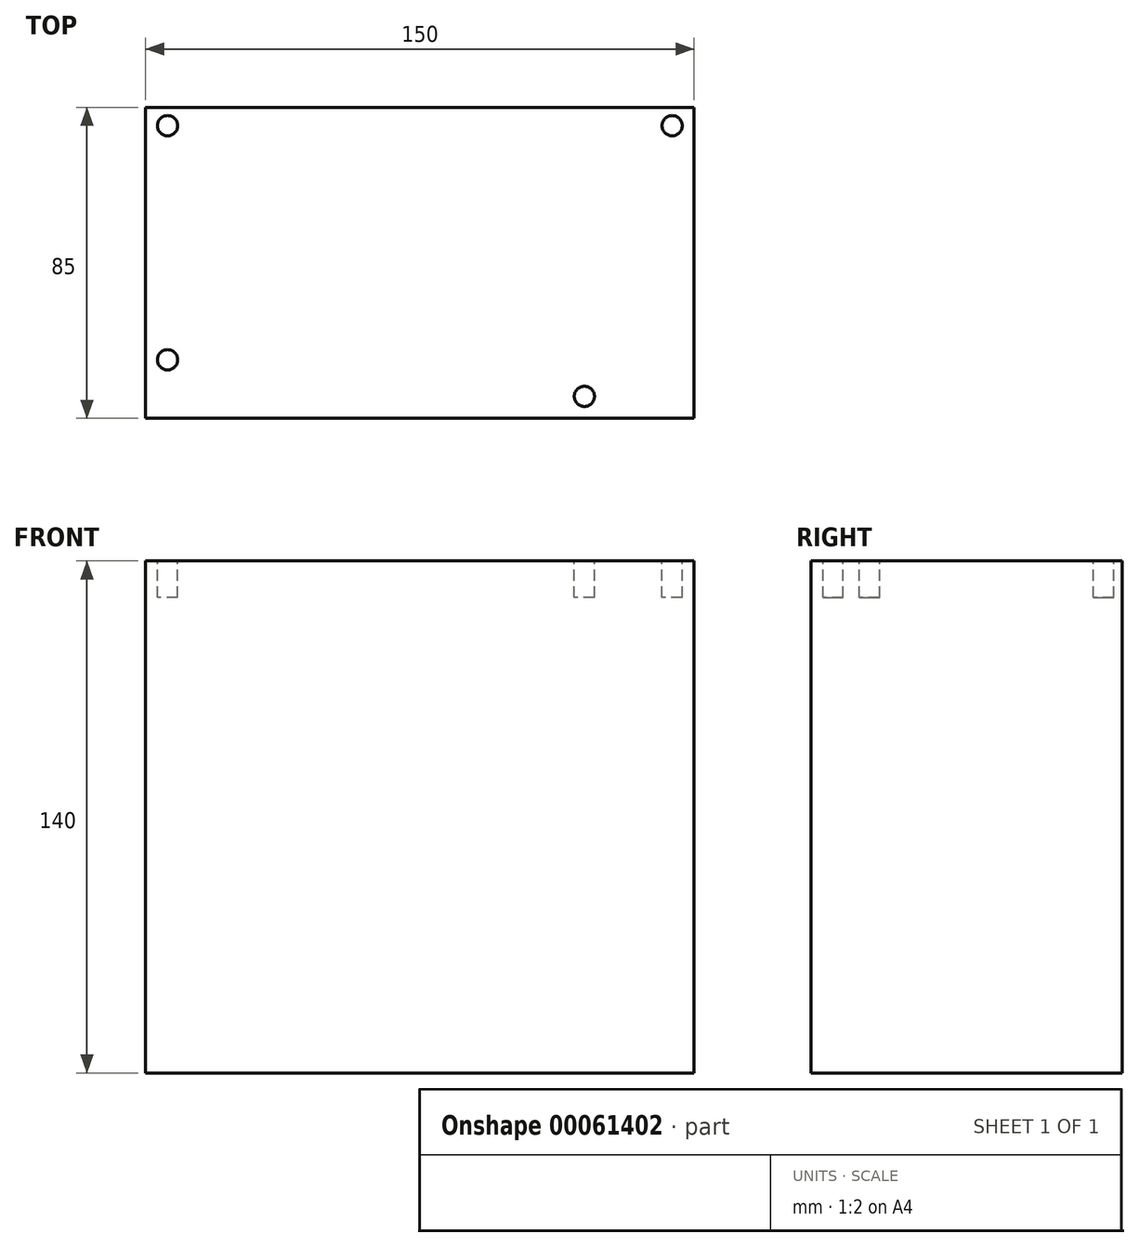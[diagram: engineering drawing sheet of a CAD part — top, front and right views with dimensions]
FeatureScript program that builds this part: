
annotation { "Feature Type Name" : "Feature", "Feature Type Description" : "" }
export const myFeature = defineFeature(function(context is Context, id is Id, definition is map)
    precondition{}
    {
        {
            var Q0;
            Q0=qCreatedBy(makeId("Front.planeOp"),FACE);
            var sketch = newSketch(context, id + "F0", { "sketchPlane" : qUnion([Q0])});
            skLineSegment(sketch, "E0.bottom", {"start": v(-73.07, 66.3) * mm, "end": v(76.93, 66.3) * mm});
            skLineSegment(sketch, "E0.top", {"start": v(-73.07, -73.7) * mm, "end": v(76.93, -73.7) * mm});
            skLineSegment(sketch, "E0.left", {"start": v(-73.07, 66.3) * mm, "end": v(-73.07, -73.7) * mm});
            skLineSegment(sketch, "E0.right", {"start": v(76.93, 66.3) * mm, "end": v(76.93, -73.7) * mm});
            skSolve(sketch);
        }
        {
            var Q0;
            Q0 = qSketchRegion(id + "F0", true);
            extrude(context, id + "F1", {"entities" : qUnion([Q0]), "depth" : 85 * mm});
        }
        {
            var Q0;
            Q0=makeQuery(id+"F1.opExtrude","SWEPT_FACE",FACE,{"disambiguationData":[OSD([sQuery(id+"F0.wireOp",EDGE,"E0.bottom")])]});
            var sketch = newSketch(context, id + "F2", { "sketchPlane" : qUnion([Q0])});
            skCircle(sketch, "E1", {"center": v(-67.07, -5) * mm, "radius": 2.77 * mm});
            skCircle(sketch, "E2", {"center": v(-67.07, -69) * mm, "radius": 2.77 * mm});
            skCircle(sketch, "E3", {"center": v(70.93, -5) * mm, "radius": 2.77 * mm});
            skCircle(sketch, "E4", {"center": v(46.93, -79) * mm, "radius": 2.77 * mm});
            skSolve(sketch);
        }
        {
            var Q0;
            Q0 = qSketchRegion(id + "F2", true);
            extrude(context, id + "F3", {"entities" : qUnion([Q0]), "operationType" : NewBodyOperationType.REMOVE, "oppositeDirection" : true, "depth" : 10 * mm});
        }
    });
